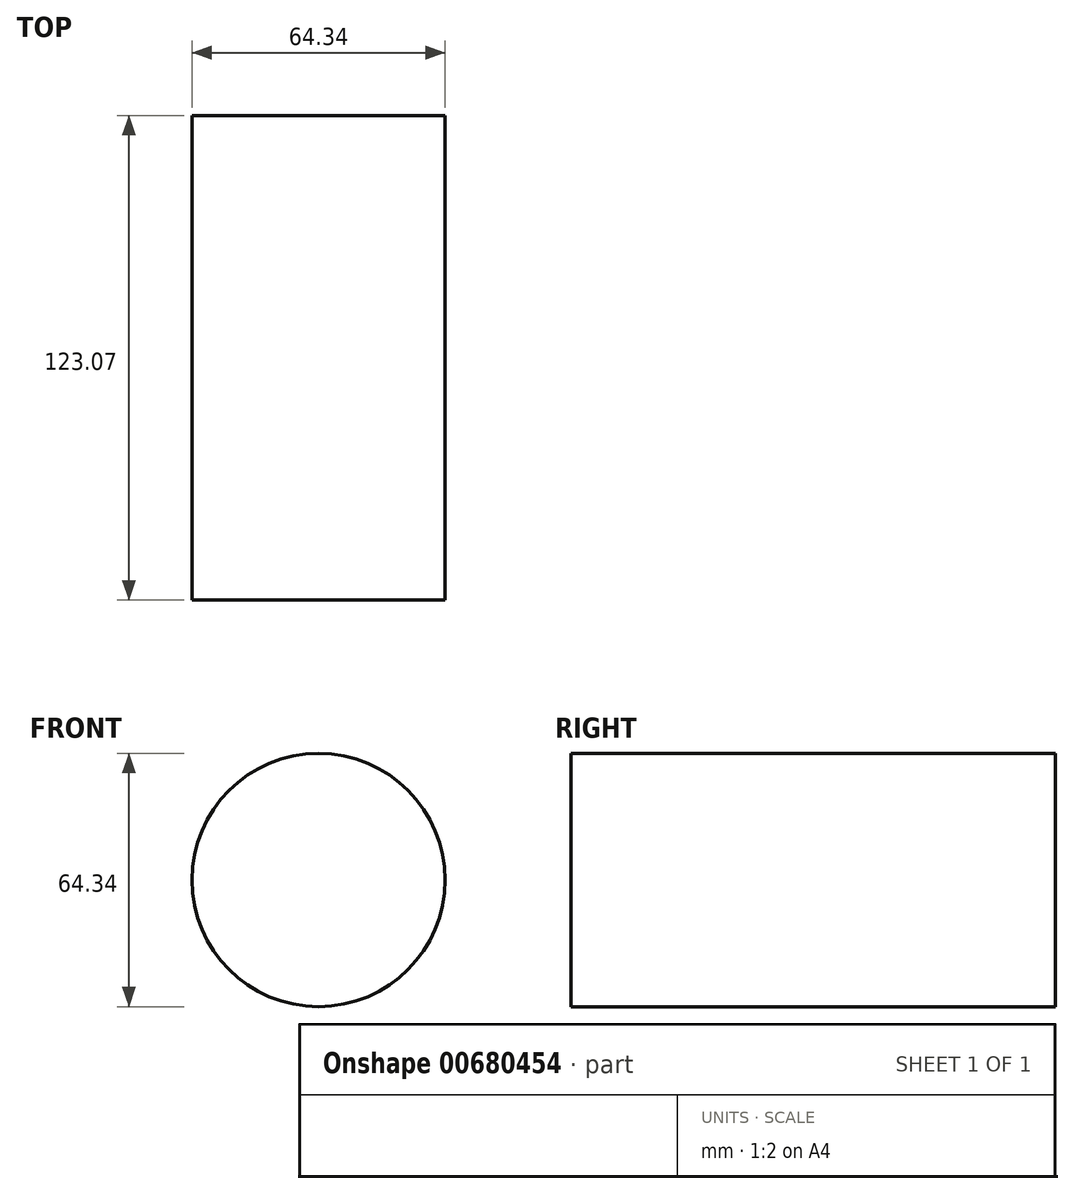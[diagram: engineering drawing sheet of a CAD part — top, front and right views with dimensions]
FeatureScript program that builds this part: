
annotation { "Feature Type Name" : "Feature", "Feature Type Description" : "" }
export const myFeature = defineFeature(function(context is Context, id is Id, definition is map)
    precondition{}
    {
        {
            var Q0;
            Q0=qCreatedBy(makeId("Front.planeOp"),FACE);
            var sketch = newSketch(context, id + "F0", { "sketchPlane" : qUnion([Q0])});
            skCircle(sketch, "E0", {"center": v(-28.03, 51.43) * mm, "radius": 32.17 * mm});
            skSolve(sketch);
        }
        {
            var Q0;
            Q0 = qSketchRegion(id + "F0", true);
            extrude(context, id + "F1", {"entities" : qUnion([Q0]), "depth" : 123.07 * mm, "offsetDistance" : 25.4 * mm});
        }
    });
